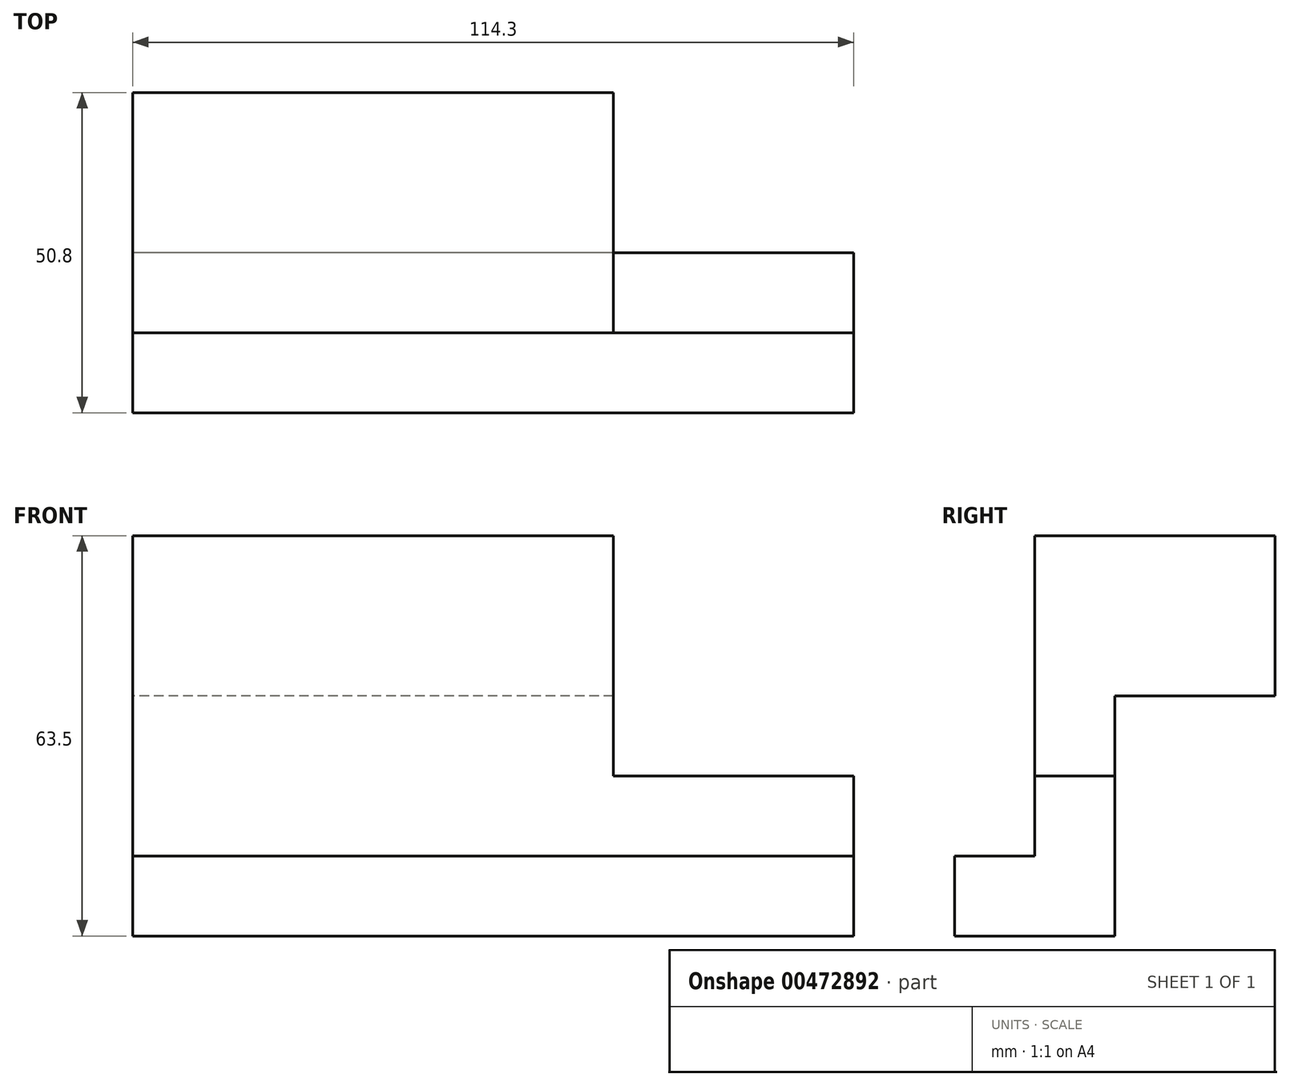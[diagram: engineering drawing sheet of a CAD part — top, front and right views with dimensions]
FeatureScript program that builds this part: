
annotation { "Feature Type Name" : "Feature", "Feature Type Description" : "" }
export const myFeature = defineFeature(function(context is Context, id is Id, definition is map)
    precondition{}
    {
        {
            var Q0;
            Q0=qCreatedBy(makeId("Front.planeOp"),FACE);
            var sketch = newSketch(context, id + "F0", { "sketchPlane" : qUnion([Q0])});
            skLineSegment(sketch, "E0", {"start": v(-32.3, 45.48) * mm, "end": v(-32.3, -18.02) * mm});
            skLineSegment(sketch, "E1", {"start": v(-32.3, -18.02) * mm, "end": v(82, -18.02) * mm});
            skLineSegment(sketch, "E2", {"start": v(82, -18.02) * mm, "end": v(82, 7.38) * mm});
            skLineSegment(sketch, "E3", {"start": v(82, 7.38) * mm, "end": v(43.9, 7.38) * mm});
            skLineSegment(sketch, "E4", {"start": v(43.9, 7.38) * mm, "end": v(43.9, 45.48) * mm});
            skLineSegment(sketch, "E5", {"start": v(43.9, 45.48) * mm, "end": v(-32.3, 45.48) * mm});
            skSolve(sketch);
        }
        {
            var Q0;
            Q0 = qSketchRegion(id + "F0", true);
            extrude(context, id + "F1", {"entities" : qUnion([Q0]), "oppositeDirection" : true, "depth" : 50.8 * mm});
        }
        {
            var Q0;
            Q0=makeQuery(id+"F1.opExtrude","SWEPT_FACE",FACE,{"disambiguationData":[OSD([sQuery(id+"F0.wireOp",EDGE,"E0")])]});
            var sketch = newSketch(context, id + "F2", { "sketchPlane" : qUnion([Q0])});
            skLineSegment(sketch, "E6", {"start": v(-12.7, 45.48) * mm, "end": v(-12.7, -5.32) * mm});
            skLineSegment(sketch, "E7", {"start": v(-12.7, -5.32) * mm, "end": v(0, -5.32) * mm});
            skLineSegment(sketch, "E8", {"start": v(0, -5.32) * mm, "end": v(0, 45.48) * mm});
            skLineSegment(sketch, "E9", {"start": v(0, 45.48) * mm, "end": v(-12.7, 45.48) * mm});
            skSolve(sketch);
        }
        {
            var Q0;
            Q0 = qSketchRegion(id + "F2", true);
            extrude(context, id + "F3", {"entities" : qUnion([Q0]), "operationType" : NewBodyOperationType.REMOVE, "oppositeDirection" : true, "depth" : 114.8 * mm});
        }
        {
            var Q0;
            Q0=makeQuery(id+"F1.opExtrude","SWEPT_FACE",FACE,{"disambiguationData":[OSD([sQuery(id+"F0.wireOp",EDGE,"E0")])]});
            var sketch = newSketch(context, id + "F4", { "sketchPlane" : qUnion([Q0])});
            skLineSegment(sketch, "E10", {"start": v(-50.8, 20.08) * mm, "end": v(-25.4, 20.08) * mm});
            skLineSegment(sketch, "E11", {"start": v(-25.4, 20.08) * mm, "end": v(-25.4, -18.02) * mm});
            skLineSegment(sketch, "E12", {"start": v(-25.4, -18.02) * mm, "end": v(-50.8, -18.02) * mm});
            skLineSegment(sketch, "E13", {"start": v(-50.8, -18.02) * mm, "end": v(-50.8, 20.08) * mm});
            skSolve(sketch);
        }
        {
            var Q0;
            Q0 = qSketchRegion(id + "F4", true);
            extrude(context, id + "F5", {"entities" : qUnion([Q0]), "operationType" : NewBodyOperationType.REMOVE, "oppositeDirection" : true, "depth" : 115.06 * mm});
        }
    });
